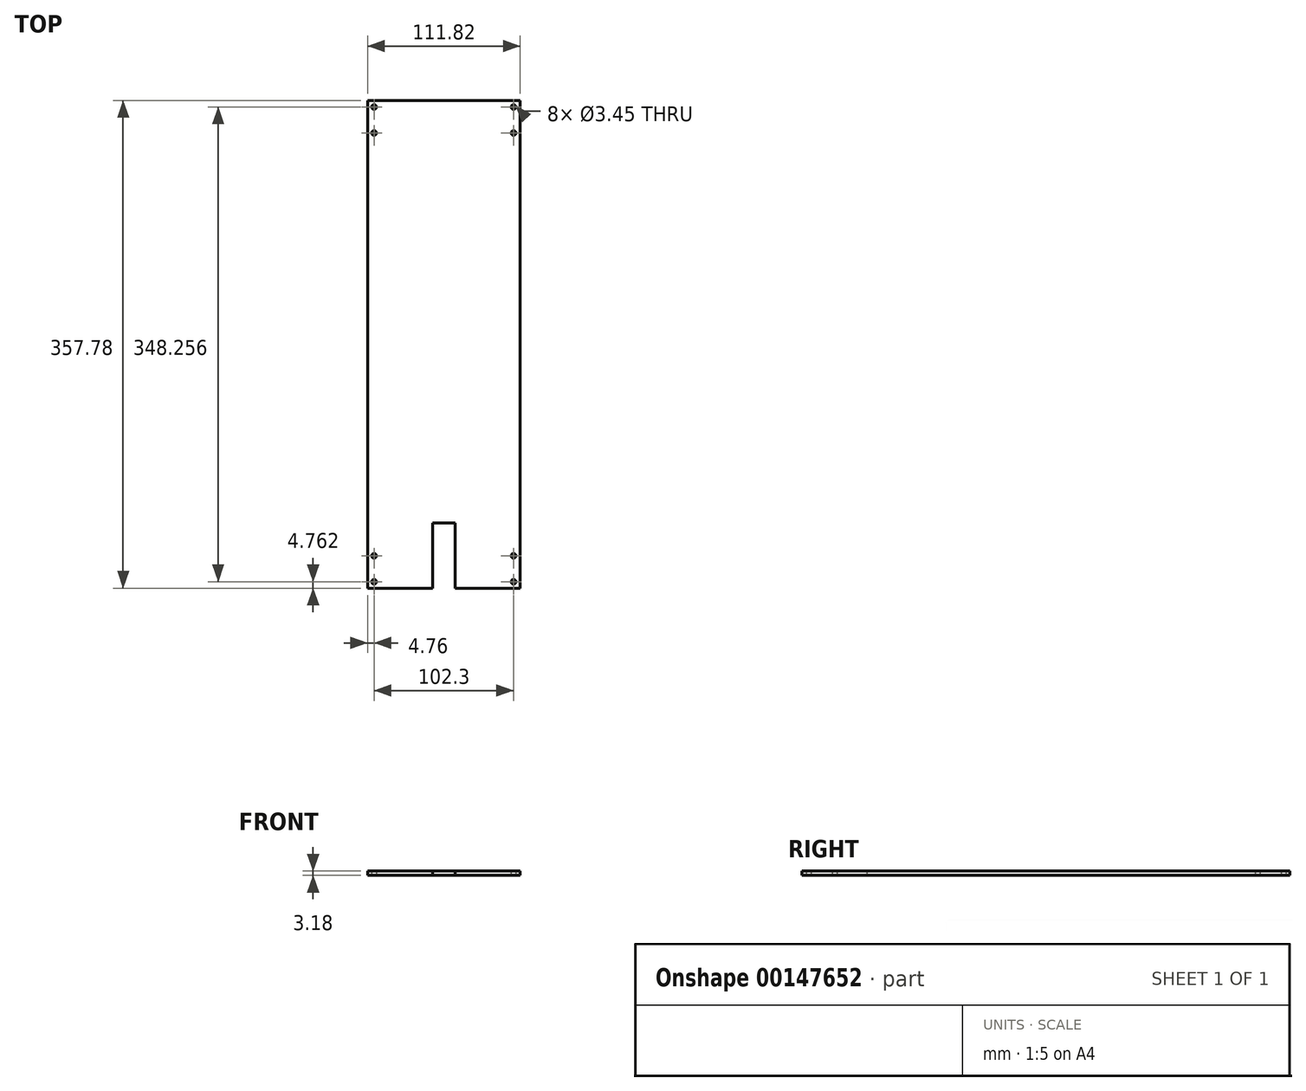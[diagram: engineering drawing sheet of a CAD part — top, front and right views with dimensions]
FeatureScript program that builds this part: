
annotation { "Feature Type Name" : "Feature", "Feature Type Description" : "" }
export const myFeature = defineFeature(function(context is Context, id is Id, definition is map)
    precondition{}
    {
        {
            var Q0;
            Q0=qCreatedBy(makeId("Top.planeOp"),FACE);
            var sketch = newSketch(context, id + "F0", { "sketchPlane" : qUnion([Q0])});
            skLineSegment(sketch, "E0.bottom", {"start": v(55.91, -178.9) * mm, "end": v(-55.91, -178.9) * mm});
            skLineSegment(sketch, "E0.top", {"start": v(55.91, 178.9) * mm, "end": v(-55.91, 178.9) * mm});
            skLineSegment(sketch, "E0.left", {"start": v(55.91, -178.9) * mm, "end": v(55.91, 178.9) * mm});
            skLineSegment(sketch, "E0.right", {"start": v(-55.91, -178.9) * mm, "end": v(-55.91, 178.9) * mm});
            skPoint(sketch, "E0.middle", {"position": v(0, 0) * mm});
            skLineSegment(sketch, "E1", {"start": v(51.15, 155.08) * mm, "end": v(55.91, 155.08) * mm, "construction": true});
            skLineSegment(sketch, "E2.bottom", {"start": v(51.15, 155.08) * mm, "end": v(-51.15, 155.08) * mm, "construction": true});
            skLineSegment(sketch, "E2.top", {"start": v(51.15, -155.08) * mm, "end": v(-51.15, -155.08) * mm, "construction": true});
            skLineSegment(sketch, "E2.left", {"start": v(51.15, 155.08) * mm, "end": v(51.15, -155.08) * mm, "construction": true});
            skLineSegment(sketch, "E2.right", {"start": v(-51.15, 155.08) * mm, "end": v(-51.15, -155.08) * mm, "construction": true});
            skCircle(sketch, "E3", {"center": v(51.15, 155.08) * mm, "radius": 1.73 * mm});
            skCircle(sketch, "E4", {"center": v(-51.15, -155.08) * mm, "radius": 1.73 * mm});
            skLineSegment(sketch, "E5", {"start": v(0, 155.08) * mm, "end": v(0, 178.9) * mm, "construction": true});
            skLineSegment(sketch, "E6", {"start": v(51.15, 155.08) * mm, "end": v(51.15, 174.13) * mm, "construction": true});
            skCircle(sketch, "E7", {"center": v(-51.15, 155.08) * mm, "radius": 1.73 * mm});
            skCircle(sketch, "E8", {"center": v(51.15, -155.08) * mm, "radius": 1.73 * mm});
            skLineSegment(sketch, "E9", {"start": v(51.15, 174.13) * mm, "end": v(51.15, 178.9) * mm, "construction": true});
            skCircle(sketch, "E10", {"center": v(51.15, 174.13) * mm, "radius": 1.73 * mm});
            skLineSegment(sketch, "E11", {"start": v(-51.15, 155.08) * mm, "end": v(-51.15, 174.13) * mm, "construction": true});
            skLineSegment(sketch, "E12", {"start": v(-51.15, 174.13) * mm, "end": v(-51.15, 178.9) * mm, "construction": true});
            skLineSegment(sketch, "E13", {"start": v(-51.15, -155.08) * mm, "end": v(-51.15, -174.13) * mm, "construction": true});
            skLineSegment(sketch, "E14", {"start": v(-51.15, -174.13) * mm, "end": v(-51.15, -178.9) * mm, "construction": true});
            skLineSegment(sketch, "E15", {"start": v(51.15, -155.08) * mm, "end": v(51.15, -174.13) * mm, "construction": true});
            skLineSegment(sketch, "E16", {"start": v(51.15, -174.13) * mm, "end": v(51.15, -178.9) * mm, "construction": true});
            skCircle(sketch, "E17", {"center": v(-51.15, 174.13) * mm, "radius": 1.73 * mm});
            skCircle(sketch, "E18", {"center": v(-51.15, -174.13) * mm, "radius": 1.73 * mm});
            skCircle(sketch, "E19", {"center": v(51.15, -174.13) * mm, "radius": 1.73 * mm});
            skSolve(sketch);
        }
        {
            var Q0;
            Q0=makeQuery(id+"F0.imprint","IMPRINT",FACE,{"disambiguationData":[TD([[makeQuery(id+"F0.imprint","IMPRINT",EDGE,{"derivedFrom":sQuery(id+"F0.wireOp",EDGE,"E0.bottom")}),-1.0]])]});
            extrude(context, id + "F1", {"entities" : qUnion([Q0]), "depth" : 3.17 * mm});
        }
        {
            var Q0;
            Q0=makeQuery(id+"F1.opExtrude","CAP_FACE",FACE,{"disambiguationData":[OSD([sQuery(id+"F0.wireOp",EDGE,"E0.bottom"),sQuery(id+"F0.wireOp",EDGE,"E0.top"),sQuery(id+"F0.wireOp",EDGE,"E0.left"),sQuery(id+"F0.wireOp",EDGE,"E0.right"),sQuery(id+"F0.wireOp",EDGE,"E3"),sQuery(id+"F0.wireOp",EDGE,"E4"),sQuery(id+"F0.wireOp",EDGE,"E7"),sQuery(id+"F0.wireOp",EDGE,"E8"),sQuery(id+"F0.wireOp",EDGE,"E10"),sQuery(id+"F0.wireOp",EDGE,"E17"),sQuery(id+"F0.wireOp",EDGE,"E18"),sQuery(id+"F0.wireOp",EDGE,"E19")])],"isStart":false});
            var sketch = newSketch(context, id + "F2", { "sketchPlane" : qUnion([Q0])});
            skLineSegment(sketch, "E20.bottom", {"start": v(-8.26, -178.9) * mm, "end": v(8.25, -178.9) * mm});
            skLineSegment(sketch, "E20.top", {"start": v(-8.26, -130.99) * mm, "end": v(8.25, -130.99) * mm});
            skLineSegment(sketch, "E20.left", {"start": v(-8.26, -178.9) * mm, "end": v(-8.26, -130.99) * mm});
            skLineSegment(sketch, "E20.right", {"start": v(8.25, -178.9) * mm, "end": v(8.25, -130.99) * mm});
            skPoint(sketch, "E21", {"position": v(0, -178.9) * mm});
            skSolve(sketch);
        }
        {
            var Q0;
            Q0=qSketchRegion(id+"F2",true);
            var Q1;
            Q1=makeQuery(id+"F1.opExtrude","CAP_FACE",FACE,{"disambiguationData":[OSD([sQuery(id+"F0.wireOp",EDGE,"E0.bottom"),sQuery(id+"F0.wireOp",EDGE,"E0.top"),sQuery(id+"F0.wireOp",EDGE,"E0.left"),sQuery(id+"F0.wireOp",EDGE,"E0.right"),sQuery(id+"F0.wireOp",EDGE,"E3"),sQuery(id+"F0.wireOp",EDGE,"E4"),sQuery(id+"F0.wireOp",EDGE,"E7"),sQuery(id+"F0.wireOp",EDGE,"E8"),sQuery(id+"F0.wireOp",EDGE,"E10"),sQuery(id+"F0.wireOp",EDGE,"E17"),sQuery(id+"F0.wireOp",EDGE,"E18"),sQuery(id+"F0.wireOp",EDGE,"E19")])],"isStart":true});
            extrude(context, id + "F3", {"entities" : qUnion([Q0]), "operationType" : NewBodyOperationType.REMOVE, "endBound" : BoundingType.UP_TO_SURFACE, "oppositeDirection" : true, "endBoundEntityFace" : qUnion([Q1]), "depth" : 25.4 * mm});
        }
    });
